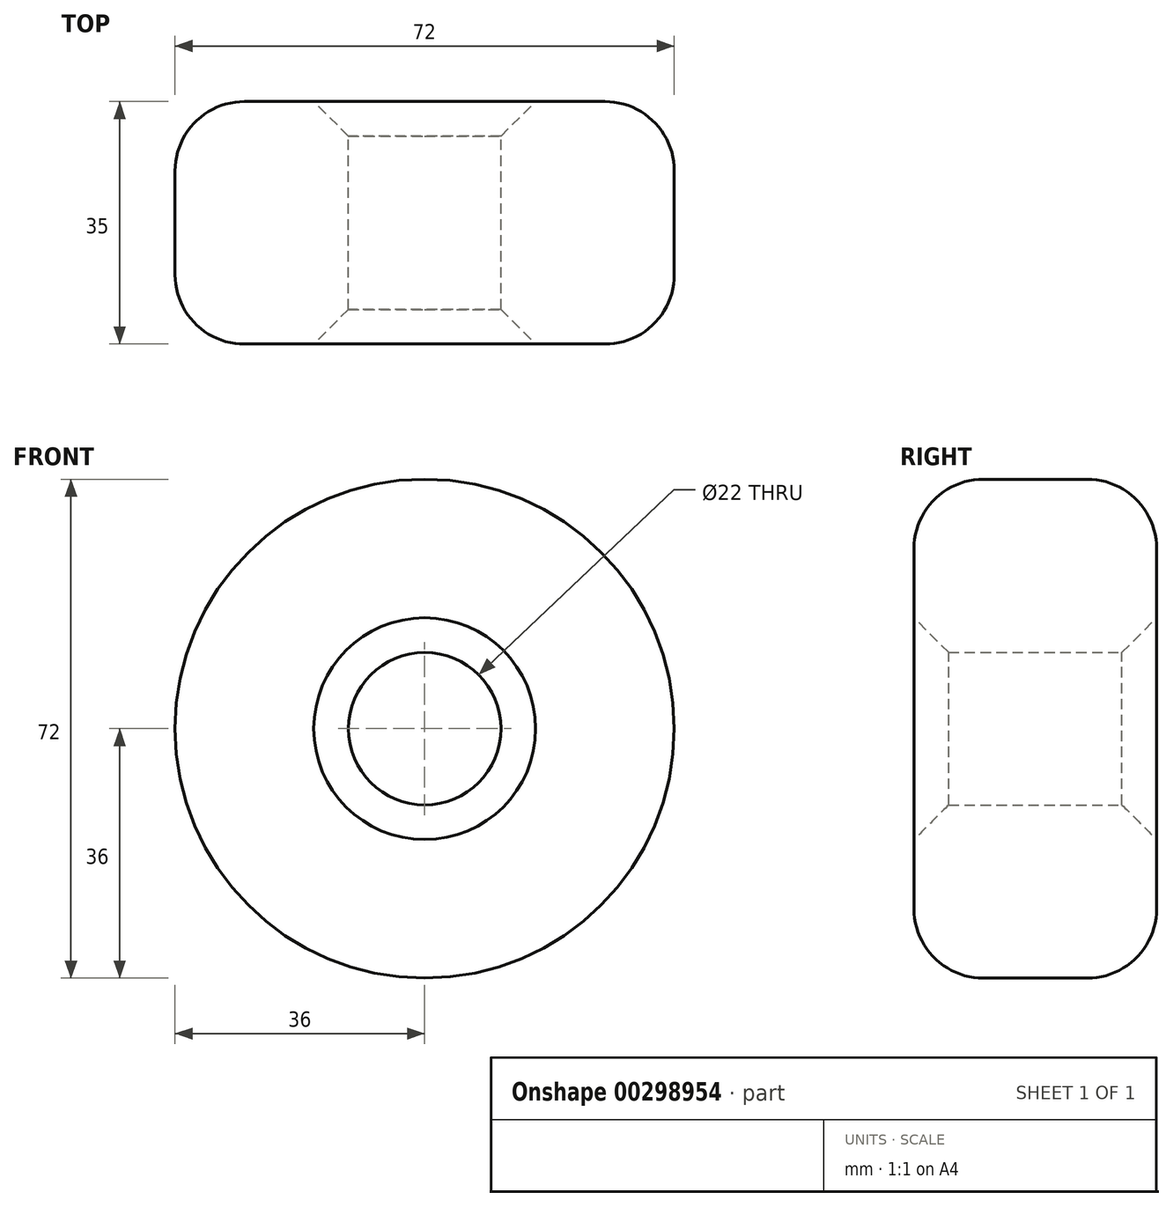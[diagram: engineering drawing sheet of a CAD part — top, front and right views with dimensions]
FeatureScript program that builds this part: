
annotation { "Feature Type Name" : "Feature", "Feature Type Description" : "" }
export const myFeature = defineFeature(function(context is Context, id is Id, definition is map)
    precondition{}
    {
        {
            var Q0;
            Q0=qCreatedBy(makeId("Front.planeOp"),FACE);
            var sketch = newSketch(context, id + "F0", { "sketchPlane" : qUnion([Q0])});
            skCircle(sketch, "E0", {"center": v(0, 0) * mm, "radius": 36 * mm});
            skCircle(sketch, "E1", {"center": v(0, 0) * mm, "radius": 11 * mm});
            skSolve(sketch);
        }
        {
            var Q0;
            Q0=qSketchRegion(id+"F0",true);
            extrude(context, id + "F1", {"entities" : qUnion([Q0]), "endBound" : BoundingType.SYMMETRIC, "depth" : 35 * mm});
        }
        {
            var Q0;
            Q0=makeQuery(id+"F1.opExtrude","CAP_EDGE",EDGE,{"disambiguationData":[OSD([sQuery(id+"F0.wireOp",EDGE,"E0")])],"isStart":false});
            var Q1;
            Q1=makeQuery(id+"F1.opExtrude","CAP_EDGE",EDGE,{"disambiguationData":[OSD([sQuery(id+"F0.wireOp",EDGE,"E0")])],"isStart":true});
            fillet(context, id + "F2", {"entities" : qUnion([Q0, Q1]), "radius" : 10 * mm, "tangentPropagation" : true, "allowEdgeOverflow" : false});
        }
        {
            var Q0;
            Q0=makeQuery(id+"F1.opExtrude","SWEPT_FACE",FACE,{"disambiguationData":[OSD([sQuery(id+"F0.wireOp",EDGE,"E0")])]});
            var Q1;
            Q1=makeQuery(id+"F1.opExtrude","CAP_EDGE",EDGE,{"disambiguationData":[OSD([sQuery(id+"F0.wireOp",EDGE,"E1")])],"isStart":false});
            var Q2;
            Q2=makeQuery(id+"F1.opExtrude","CAP_EDGE",EDGE,{"disambiguationData":[OSD([sQuery(id+"F0.wireOp",EDGE,"E1")])],"isStart":true});
            chamfer(context, id + "F3", {"entities" : qUnion([Q0, Q1, Q2]), "width" : 5 * mm, "tangentPropagation" : true});
        }
    });
